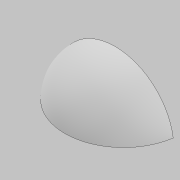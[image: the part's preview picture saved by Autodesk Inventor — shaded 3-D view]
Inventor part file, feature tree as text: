
AUTODESK INVENTOR PART (.ipt)
format: ipt  version: 2021 (Build 250183000, 183)  size: 120,320 bytes
history: native  units: mm
features: other x3, revolve x1, sketch x1
ambient origin geometry x8: Origin, YZ Plane, XZ Plane, XY Plane, X Axis, Y Axis, Z Axis, Center Point
bodies: Body1 (feature_tree)
feature tree (5):
  revolve  "Revolution2"  [1 undecoded]
  other  "midPlane"
  sketch  "Sketch1"  dims[d0=0.0mm d1=0.0mm d2=0.0mm d3=150.0mm d6=900.0mm d8=1039.230485mm d10=0.0mm d11=10.0mm d12=0.0mm d13=90.0deg d9=0.872665mm]
  other  "end1"
  other  "end2"
note: 1 required parameter value undecoded (feature->parameter linkage not recoverable at this tier; creation-order binding heuristic only, values carry confidence <= 0.55)
